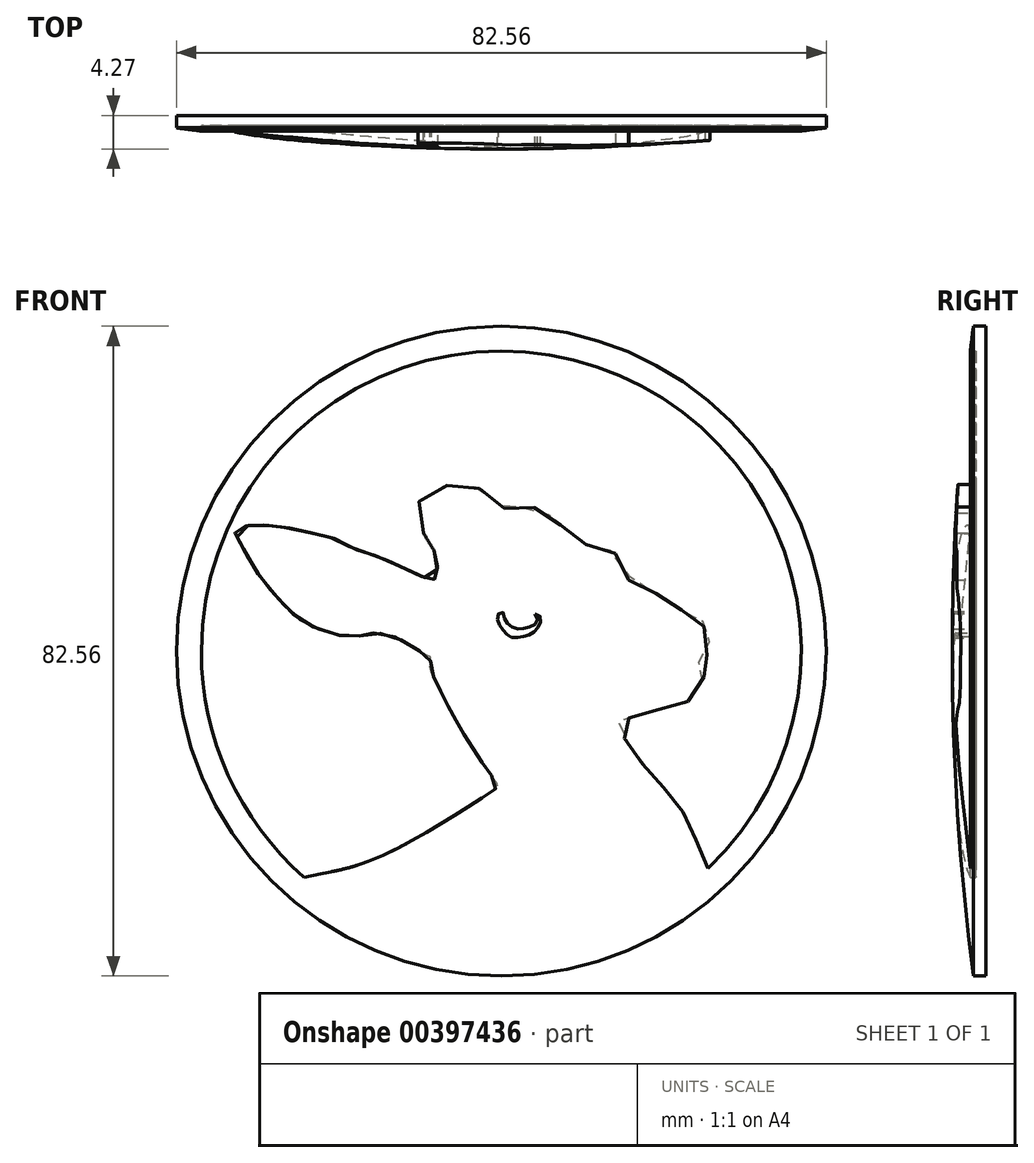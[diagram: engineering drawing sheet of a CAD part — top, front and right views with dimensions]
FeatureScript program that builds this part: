
annotation { "Feature Type Name" : "Feature", "Feature Type Description" : "" }
export const myFeature = defineFeature(function(context is Context, id is Id, definition is map)
    precondition{}
    {
        {
            var Q0;
            Q0=qCreatedBy(makeId("Front.planeOp"),FACE);
            var sketch = newSketch(context, id + "F0", { "sketchPlane" : qUnion([Q0])});
            skCircle(sketch, "E0", {"center": v(0, 0) * mm, "radius": 41.28 * mm});
            skArc(sketch, "E1", {"start": v(26.24, -27.62) * mm, "mid": v(-0.81, 38.1) * mm, "end": v(-25.04, -28.72) * mm});
            skFitSpline(sketch, "E2", {"points": [v(-25.04, -28.72) * mm, v(-19.48, -27.54) * mm, v(-15.76, -26.26) * mm, v(-8.94, -22.7) * mm, v(-0.69, -17.46) * mm, v(-0.42, -17.12) * mm, v(-1.46, -15.57) * mm, v(-5.53, -9.2) * mm, v(-8.65, -3.17) * mm, v(-9.09, -1.69) * mm, v(-8.96, -0.76) * mm, v(-9.42, -0.55) * mm, v(-13.39, 1.73) * mm, v(-16.57, 2.26) * mm, v(-17.81, 1.99) * mm, v(-20.48, 1.99) * mm, v(-25.2, 3.78) * mm, v(-27.97, 6.3) * mm, v(-31.6, 10.88) * mm, v(-33.62, 14.64) * mm, v(-33.83, 15.24) * mm, v(-32.28, 15.93) * mm, v(-29.96, 16) * mm, v(-26.45, 15.54) * mm, v(-21.66, 14.43) * mm, v(-20.18, 13.92) * mm, v(-19.36, 13.25) * mm, v(-18.27, 12.83) * mm, v(-15.76, 12.03) * mm, v(-11.28, 10.03) * mm, v(-8.96, 9.09) * mm, v(-8.44, 9.17) * mm, v(-8.19, 10.33) * mm, v(-8.1, 11.8) * mm, v(-10.4, 16.16) * mm, v(-10.54, 18.44) * mm, v(-10.4, 19.1) * mm, v(-9.07, 20.17) * mm, v(-7.59, 20.88) * mm, v(-5.78, 21.18) * mm, v(-3.7, 20.95) * mm, v(-2.02, 20.31) * mm, v(-0.35, 19.06) * mm, v(0.8, 17.6) * mm, v(0.95, 17.56) * mm, v(2.35, 18.16) * mm, v(3.8, 18.3) * mm, v(5.1, 17.95) * mm, v(7.08, 16.4) * mm, v(10.74, 13.55) * mm, v(11.8, 13.26) * mm, v(12.99, 13.14) * mm, v(14.47, 12.41) * mm, v(15.72, 11) * mm, v(16.2, 9.04) * mm, v(16.2, 8.88) * mm, v(19, 7.57) * mm, v(21.87, 6.11) * mm, v(23.14, 5) * mm, v(24.35, 4.42) * mm, v(25.18, 4.19) * mm, v(25.58, 3.76) * mm, v(25.88, 2.33) * mm, v(26, 1.76) * mm, v(26.41, 1.13) * mm, v(26.08, -0.62) * mm, v(25.14, -1.34) * mm, v(25.04, -1.4) * mm, v(25.41, -1.65) * mm, v(25.83, -1.94) * mm, v(25.9, -2.74) * mm, v(24.7, -5.28) * mm, v(24.23, -6.01) * mm, v(22.89, -6.88) * mm, v(22.32, -7.15) * mm, v(20.2, -7.35) * mm, v(18.96, -7.67) * mm, v(14.82, -8.98) * mm, v(14.57, -9.22) * mm, v(14.84, -9.8) * mm, v(16.72, -12.75) * mm, v(18.35, -14.8) * mm, v(21, -17.8) * mm, v(22.31, -19.24) * mm, v(23.7, -21.67) * mm, v(24.65, -23.82) * mm, v(25.96, -26.56) * mm, v(26.24, -27.62) * mm], "startDerivative": vector(307.78, 58.23) * mm, "endDerivative": vector(-8.2, -128.45) * mm});
            skFitSpline(sketch, "E3", {"points": [v(7.61, 4.1) * mm, v(7.76, 3.95) * mm, v(7.53, 3.6) * mm, v(7.12, 3.3) * mm, v(6.3, 3.32) * mm, v(5.43, 2.76) * mm, v(4.57, 1.97) * mm, v(3.23, 1.3) * mm, v(2.38, 1) * mm, v(1.13, 1.18) * mm, v(-0.37, 2.16) * mm, v(-1.35, 3.63) * mm, v(-1.41, 4.95) * mm, v(-0.53, 5.93) * mm, v(0.88, 6.43) * mm, v(2.12, 6.48) * mm, v(3.5, 6.23) * mm, v(4.7, 5.58) * mm, v(6.06, 4.78) * mm, v(7.34, 4.28) * mm, v(7.61, 4.1) * mm]});
            skFitSpline(sketch, "E4", {"points": [v(4.29, 4.74) * mm, v(4.4, 4.77) * mm, v(4.71, 4.64) * mm, v(4.96, 4.34) * mm, v(4.92, 3.58) * mm, v(4.44, 2.72) * mm, v(3.67, 2.08) * mm, v(2.04, 1.72) * mm, v(1.14, 1.8) * mm, v(0.28, 2.6) * mm, v(-0.27, 3.42) * mm, v(-0.49, 4.38) * mm, v(-0.26, 4.87) * mm, v(0.13, 5.03) * mm, v(0.35, 4.38) * mm, v(0.77, 3.58) * mm, v(1.58, 2.94) * mm, v(2.58, 2.85) * mm, v(3.73, 3.14) * mm, v(4.4, 3.5) * mm, v(4.57, 4.26) * mm, v(4.29, 4.74) * mm]});
            skFitSpline(sketch, "E5", {"points": [v(-22.37, -30.84) * mm, v(-19.06, -30.05) * mm, v(-15.02, -28.49) * mm, v(-10.4, -26) * mm, v(-3.68, -21.58) * mm, v(0, -19.17) * mm, v(1.47, -17.4) * mm, v(-0.94, -13.43) * mm, v(-4.66, -7.43) * mm, v(-6.74, -3.2) * mm, v(-7.35, -2.03) * mm, v(-7.39, -1.17) * mm, v(-7.35, -0.73) * mm, v(-8.38, 0.38) * mm, v(-12.32, 2.77) * mm, v(-15.16, 3.59) * mm, v(-16.7, 3.52) * mm, v(-17.86, 3.23) * mm, v(-20.3, 3.23) * mm, v(-24.02, 4.56) * mm, v(-26.73, 6.75) * mm, v(-30.35, 11.24) * mm, v(-32.7, 14.82) * mm, v(-32.72, 14.95) * mm, v(-31.6, 14.97) * mm, v(-30.04, 14.83) * mm, v(-26.9, 14.5) * mm, v(-21.8, 13.49) * mm, v(-20.59, 12.89) * mm, v(-19.8, 12.42) * mm, v(-18.5, 11.96) * mm, v(-16.07, 11.02) * mm, v(-11.76, 9.16) * mm, v(-9.22, 8.17) * mm, v(-8.23, 8.06) * mm, v(-7.68, 8.7) * mm, v(-7.35, 10.26) * mm, v(-7.34, 11.76) * mm, v(-9.32, 16.25) * mm, v(-9.58, 18.37) * mm, v(-9.54, 18.93) * mm, v(-8.79, 19.48) * mm, v(-7.4, 19.95) * mm, v(-5.77, 20.22) * mm, v(-3.9, 19.99) * mm, v(-2.46, 19.33) * mm, v(-0.88, 18.08) * mm, v(0, 17.04) * mm, v(0.41, 16.75) * mm, v(0.97, 16.67) * mm, v(2.45, 17.39) * mm, v(3.78, 17.54) * mm, v(4.85, 17.15) * mm, v(6.6, 15.64) * mm, v(10.08, 12.83) * mm, v(11.49, 12.38) * mm], "startDerivative": vector(145.84, 28.8) * mm, "endDerivative": vector(75.2, -19.94) * mm});
            skFitSpline(sketch, "E6", {"points": [v(11.27, 12.43) * mm, v(11.73, 12.38) * mm, v(12.77, 12.3) * mm, v(14.15, 11.64) * mm, v(14.93, 10.76) * mm, v(15.26, 9.23) * mm, v(15.3, 9.06) * mm, v(15.41, 8.76) * mm, v(15.6, 8.42) * mm, v(16.27, 7.98) * mm, v(18.58, 6.97) * mm, v(20.1, 6.23) * mm, v(21.4, 5.5) * mm, v(22.62, 4.48) * mm, v(23.75, 3.76) * mm, v(24.41, 3.73) * mm, v(25, 3.45) * mm, v(25.05, 2.53) * mm, v(25.12, 2.01) * mm, v(25.32, 1.64) * mm, v(25.61, 1.2) * mm, v(25.6, 0.46) * mm, v(24.47, -0.73) * mm, v(24.47, -0.73) * mm, v(24.74, -2.37) * mm, v(25.06, -2.72) * mm, v(23.98, -4.64) * mm, v(23.19, -5.37) * mm, v(22.2, -5.97) * mm, v(20.6, -6.19) * mm, v(17.5, -6.96) * mm, v(14.1, -8.03) * mm, v(13.42, -8.73) * mm, v(13.71, -9.85) * mm, v(15.55, -12.9) * mm, v(17.2, -15.16) * mm, v(19.65, -18.24) * mm, v(20.92, -19.6) * mm, v(21.7, -21.35) * mm, v(23.01, -24.18) * mm, v(25.16, -28.62) * mm], "startDerivative": vector(29.37, -4.86) * mm, "endDerivative": vector(48.2, -100.57) * mm});
            skFitSpline(sketch, "E7", {"points": [v(24.47, -0.73) * mm, v(22.07, -1.86) * mm, v(19.33, -2.71) * mm, v(16.82, -3.03) * mm, v(16.33, -3) * mm, v(16.2, -3.27) * mm, v(16.6, -3.47) * mm, v(17.9, -3.75) * mm, v(19.7, -3.49) * mm, v(23.51, -2.3) * mm, v(24.1, -2.25) * mm, v(24.74, -2.37) * mm], "startDerivative": vector(-12.18, -5.86) * mm, "endDerivative": vector(10.98, -2.26) * mm});
            skFitSpline(sketch, "E8", {"points": [v(-7.6, 12.49) * mm, v(-6.5, 15) * mm, v(-4.52, 16.15) * mm, v(-1.07, 17.04) * mm, v(-1.45, 17.55) * mm, v(-4.69, 17.28) * mm, v(-6.94, 16.18) * mm, v(-8.17, 14.26) * mm, v(-8.58, 12.8) * mm], "startDerivative": vector(6.1, 20.33) * mm, "endDerivative": vector(1.86, -15.1) * mm});
            skFitSpline(sketch, "E9.trimOffspring", {"points": [v(-22.37, -30.84) * mm, v(-19.06, -30.05) * mm, v(-15.02, -28.49) * mm, v(-10.4, -26) * mm, v(-3.68, -21.58) * mm, v(0, -19.17) * mm, v(1.47, -17.4) * mm, v(-0.94, -13.43) * mm, v(-4.66, -7.43) * mm, v(-6.74, -3.2) * mm, v(-7.35, -2.03) * mm, v(-7.39, -1.17) * mm, v(-7.35, -0.73) * mm, v(-8.38, 0.38) * mm, v(-12.32, 2.77) * mm, v(-15.16, 3.59) * mm, v(-16.7, 3.52) * mm, v(-17.86, 3.23) * mm, v(-20.3, 3.23) * mm, v(-24.02, 4.56) * mm, v(-26.73, 6.75) * mm, v(-30.35, 11.24) * mm, v(-32.7, 14.82) * mm, v(-32.72, 14.95) * mm, v(-31.6, 14.97) * mm, v(-30.04, 14.83) * mm, v(-26.9, 14.5) * mm, v(-21.8, 13.49) * mm, v(-20.59, 12.89) * mm, v(-19.8, 12.42) * mm, v(-18.5, 11.96) * mm, v(-16.07, 11.02) * mm, v(-11.76, 9.16) * mm, v(-9.22, 8.17) * mm, v(-8.23, 8.06) * mm, v(-7.68, 8.7) * mm, v(-7.35, 10.26) * mm, v(-7.34, 11.76) * mm, v(-9.32, 16.25) * mm, v(-9.58, 18.37) * mm, v(-9.54, 18.93) * mm, v(-8.79, 19.48) * mm, v(-7.4, 19.95) * mm, v(-5.77, 20.22) * mm, v(-3.9, 19.99) * mm, v(-2.46, 19.33) * mm, v(-0.88, 18.08) * mm, v(0, 17.04) * mm, v(0.41, 16.75) * mm, v(0.97, 16.67) * mm, v(2.45, 17.39) * mm, v(3.78, 17.54) * mm, v(4.85, 17.15) * mm, v(6.6, 15.64) * mm, v(10.08, 12.83) * mm, v(11.49, 12.38) * mm], "startDerivative": vector(145.84, 28.8) * mm, "endDerivative": vector(75.2, -19.94) * mm});
            skFitSpline(sketch, "E10.trimOffspring", {"points": [v(-25.04, -28.72) * mm, v(-19.48, -27.54) * mm, v(-15.76, -26.26) * mm, v(-8.94, -22.7) * mm, v(-0.69, -17.46) * mm, v(-0.42, -17.12) * mm, v(-1.46, -15.57) * mm, v(-5.53, -9.2) * mm, v(-8.65, -3.17) * mm, v(-9.09, -1.69) * mm, v(-8.96, -0.76) * mm, v(-9.42, -0.55) * mm, v(-13.39, 1.73) * mm, v(-16.57, 2.26) * mm, v(-17.81, 1.99) * mm, v(-20.48, 1.99) * mm, v(-25.2, 3.78) * mm, v(-27.97, 6.3) * mm, v(-31.6, 10.88) * mm, v(-33.62, 14.64) * mm, v(-33.83, 15.24) * mm, v(-32.28, 15.93) * mm, v(-29.96, 16) * mm, v(-26.45, 15.54) * mm, v(-21.66, 14.43) * mm, v(-20.18, 13.92) * mm, v(-19.36, 13.25) * mm, v(-18.27, 12.83) * mm, v(-15.76, 12.03) * mm, v(-11.28, 10.03) * mm, v(-8.96, 9.09) * mm, v(-8.44, 9.17) * mm, v(-8.19, 10.33) * mm, v(-8.1, 11.8) * mm, v(-10.4, 16.16) * mm, v(-10.54, 18.44) * mm, v(-10.4, 19.1) * mm, v(-9.07, 20.17) * mm, v(-7.59, 20.88) * mm, v(-5.78, 21.18) * mm, v(-3.7, 20.95) * mm, v(-2.02, 20.31) * mm, v(-0.35, 19.06) * mm, v(0.8, 17.6) * mm, v(0.95, 17.56) * mm, v(2.35, 18.16) * mm, v(3.8, 18.3) * mm, v(5.1, 17.95) * mm, v(7.08, 16.4) * mm, v(10.74, 13.55) * mm, v(11.8, 13.26) * mm, v(12.99, 13.14) * mm, v(14.47, 12.41) * mm, v(15.72, 11) * mm, v(16.2, 9.04) * mm, v(16.2, 8.88) * mm, v(19, 7.57) * mm, v(21.87, 6.11) * mm, v(23.14, 5) * mm, v(24.35, 4.42) * mm, v(25.18, 4.19) * mm, v(25.58, 3.76) * mm, v(25.88, 2.33) * mm, v(26, 1.76) * mm, v(26.41, 1.13) * mm, v(26.08, -0.62) * mm, v(25.14, -1.34) * mm, v(25.04, -1.4) * mm, v(25.41, -1.65) * mm, v(25.83, -1.94) * mm, v(25.9, -2.74) * mm, v(24.7, -5.28) * mm, v(24.23, -6.01) * mm, v(22.89, -6.88) * mm, v(22.32, -7.15) * mm, v(20.2, -7.35) * mm, v(18.96, -7.67) * mm, v(14.82, -8.98) * mm, v(14.57, -9.22) * mm, v(14.84, -9.8) * mm, v(16.72, -12.75) * mm, v(18.35, -14.8) * mm, v(21, -17.8) * mm, v(22.31, -19.24) * mm, v(23.7, -21.67) * mm, v(24.65, -23.82) * mm, v(25.96, -26.56) * mm, v(26.24, -27.62) * mm], "startDerivative": vector(307.78, 58.23) * mm, "endDerivative": vector(-8.2, -128.45) * mm});
            skFitSpline(sketch, "E11", {"points": [v(-8.89, 15.15) * mm, v(-8.78, 14.88) * mm, v(-8.75, 14.71) * mm, v(-8.8, 14.54) * mm, v(-9, 14.42) * mm, v(-9.33, 14.47) * mm, v(-9.65, 14.66) * mm, v(-9.9, 15.02) * mm], "startDerivative": vector(0.8, -1.94) * mm, "endDerivative": vector(-1.2, 2.25) * mm});
            skArc(sketch, "E12.trimOffspring", {"start": v(-22.37, -30.84) * mm, "mid": v(1.78, -38.06) * mm, "end": v(25.16, -28.62) * mm});
            skSolve(sketch);
        }
        {
            var Q0;
            Q0=qCreatedBy(makeId("Front.planeOp"),FACE);
            var sketch = newSketch(context, id + "F1", { "sketchPlane" : qUnion([Q0])});
            skCircle(sketch, "E13", {"center": v(0, 0) * mm, "radius": 41.28 * mm});
            skSolve(sketch);
        }
        {
            var Q0;
            Q0=qSketchRegion(id+"F1",true);
            extrude(context, id + "F2", {"entities" : qUnion([Q0]), "depth" : 5.08 * mm, "hasSecondDirection" : true, "secondDirectionOppositeDirection" : true, "secondDirectionDepth" : 1.27 * mm});
        }
        {
            var Q0;
            Q0=makeQuery(id+"F0.imprint","IMPRINT",FACE,{"disambiguationData":[TD([[makeQuery(id+"F0.imprint","IMPRINT",EDGE,{"derivedFrom":sQuery(id+"F0.wireOp",EDGE,"E1")}),1.0]])]});
            var Q1;
            Q1=makeQuery(id+"F0.imprint","IMPRINT",FACE,{"disambiguationData":[TD([[makeQuery(id+"F0.imprint","IMPRINT",EDGE,{"derivedFrom":sQuery(id+"F0.wireOp",EDGE,"E4")}),-1.0]])]});
            extrude(context, id + "F3", {"entities" : qUnion([Q0, Q1]), "operationType" : NewBodyOperationType.REMOVE, "depth" : 12.2 * mm});
        }
        {
            var Q0;
            Q0=qCreatedBy(makeId("Top.planeOp"),FACE);
            var sketch = newSketch(context, id + "F4", { "sketchPlane" : qUnion([Q0])});
            skArc(sketch, "E14", {"start": v(-43.54, 0) * mm, "mid": v(-21.82, -2.25) * mm, "end": v(0, -3) * mm});
            skLineSegment(sketch, "E15", {"start": v(-64.55, 0) * mm, "end": v(-62.8, -31.58) * mm});
            skLineSegment(sketch, "E16", {"start": v(-62.8, -31.58) * mm, "end": v(0, -29.86) * mm});
            skLineSegment(sketch, "E17.trimOffspring", {"start": v(-43.54, 0) * mm, "end": v(-64.55, 0) * mm});
            skLineSegment(sketch, "E18", {"start": v(0, -3) * mm, "end": v(0, -18.69) * mm});
            skPoint(sketch, "E18.endSnap0", {"position": v(0, -3) * mm});
            skLineSegment(sketch, "E19", {"start": v(0, -18.69) * mm, "end": v(0, -29.86) * mm});
            skSolve(sketch);
        }
        {
            var Q0;
            Q0=makeQuery(id+"F4.imprint","IMPRINT",FACE,{"disambiguationData":[TD([[makeQuery(id+"F4.imprint","IMPRINT",EDGE,{"derivedFrom":sQuery(id+"F4.wireOp",EDGE,"E14")}),-1.0]])]});
            var Q1;
            Q1=sQuery(id+"F4.wireOp",EDGE,"E18");
            revolve(context, id + "F5", {"operationType" : NewBodyOperationType.REMOVE, "entities" : qUnion([Q0]), "axis" : qUnion([Q1]), "revolveType" : RevolveType.FULL, "oppositeDirection" : true});
        }
    });
